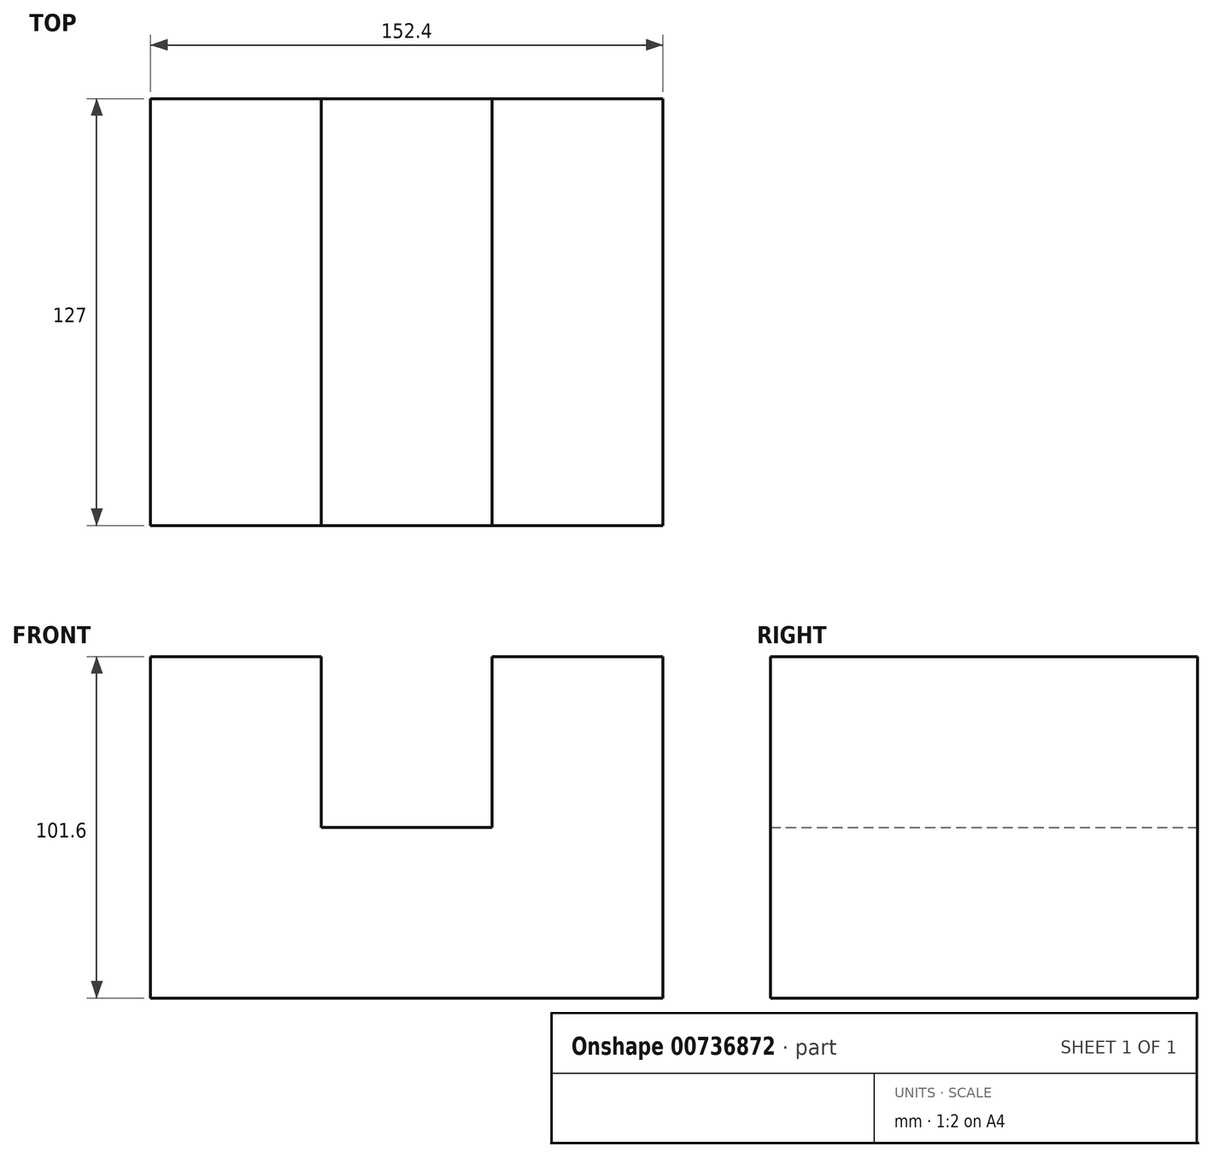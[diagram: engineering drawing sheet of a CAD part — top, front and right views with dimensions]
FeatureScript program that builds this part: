
annotation { "Feature Type Name" : "Feature", "Feature Type Description" : "" }
export const myFeature = defineFeature(function(context is Context, id is Id, definition is map)
    precondition{}
    {
        {
            var Q0;
            Q0=qCreatedBy(makeId("Front.planeOp"),FACE);
            var sketch = newSketch(context, id + "F0", { "sketchPlane" : qUnion([Q0])});
            skLineSegment(sketch, "E0", {"start": v(-77.8, -22.34) * mm, "end": v(74.6, -22.34) * mm});
            skLineSegment(sketch, "E1", {"start": v(-77.8, -22.34) * mm, "end": v(-77.8, 79.26) * mm});
            skLineSegment(sketch, "E2", {"start": v(74.6, -22.34) * mm, "end": v(74.6, 79.26) * mm});
            skLineSegment(sketch, "E3", {"start": v(-77.8, 79.26) * mm, "end": v(-27, 79.26) * mm});
            skLineSegment(sketch, "E4", {"start": v(-27, 79.26) * mm, "end": v(-27, 28.46) * mm});
            skLineSegment(sketch, "E5", {"start": v(-27, 28.46) * mm, "end": v(23.8, 28.46) * mm});
            skLineSegment(sketch, "E6", {"start": v(23.8, 28.46) * mm, "end": v(23.8, 79.26) * mm});
            skLineSegment(sketch, "E7", {"start": v(23.8, 79.26) * mm, "end": v(74.6, 79.26) * mm});
            skSolve(sketch);
        }
        {
            var Q0;
            Q0=makeQuery(id+"F0.imprint","IMPRINT",FACE,{"disambiguationData":[TD([[makeQuery(id+"F0.imprint","IMPRINT",EDGE,{"derivedFrom":sQuery(id+"F0.wireOp",EDGE,"E0")}),1.0]])]});
            extrude(context, id + "F1", {"entities" : qUnion([Q0]), "depth" : 127 * mm, "offsetDistance" : 25.4 * mm});
        }
    });
